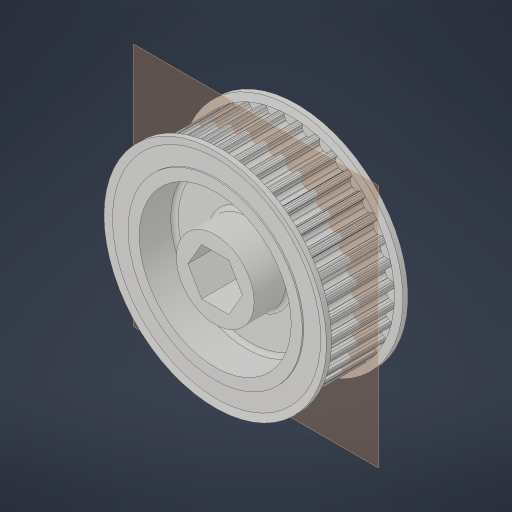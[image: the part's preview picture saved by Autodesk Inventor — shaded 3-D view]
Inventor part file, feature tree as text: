
AUTODESK INVENTOR PART (.ipt)
format: ipt  version: 2023.4 (Build 274418000, 418)  size: 887,296 bytes
history: native  units: in
note: dims shown in document units (in); Inventor stores cm internally (conversion verified against a paired STEP export)
features: mirror x1
ambient origin geometry x8: Origin, YZ Plane, XZ Plane, XY Plane, X Axis, Y Axis, Z Axis, Center Point
bodies: Solid1 (feature_tree)
feature tree (1):
  mirror  "Mirror1"
